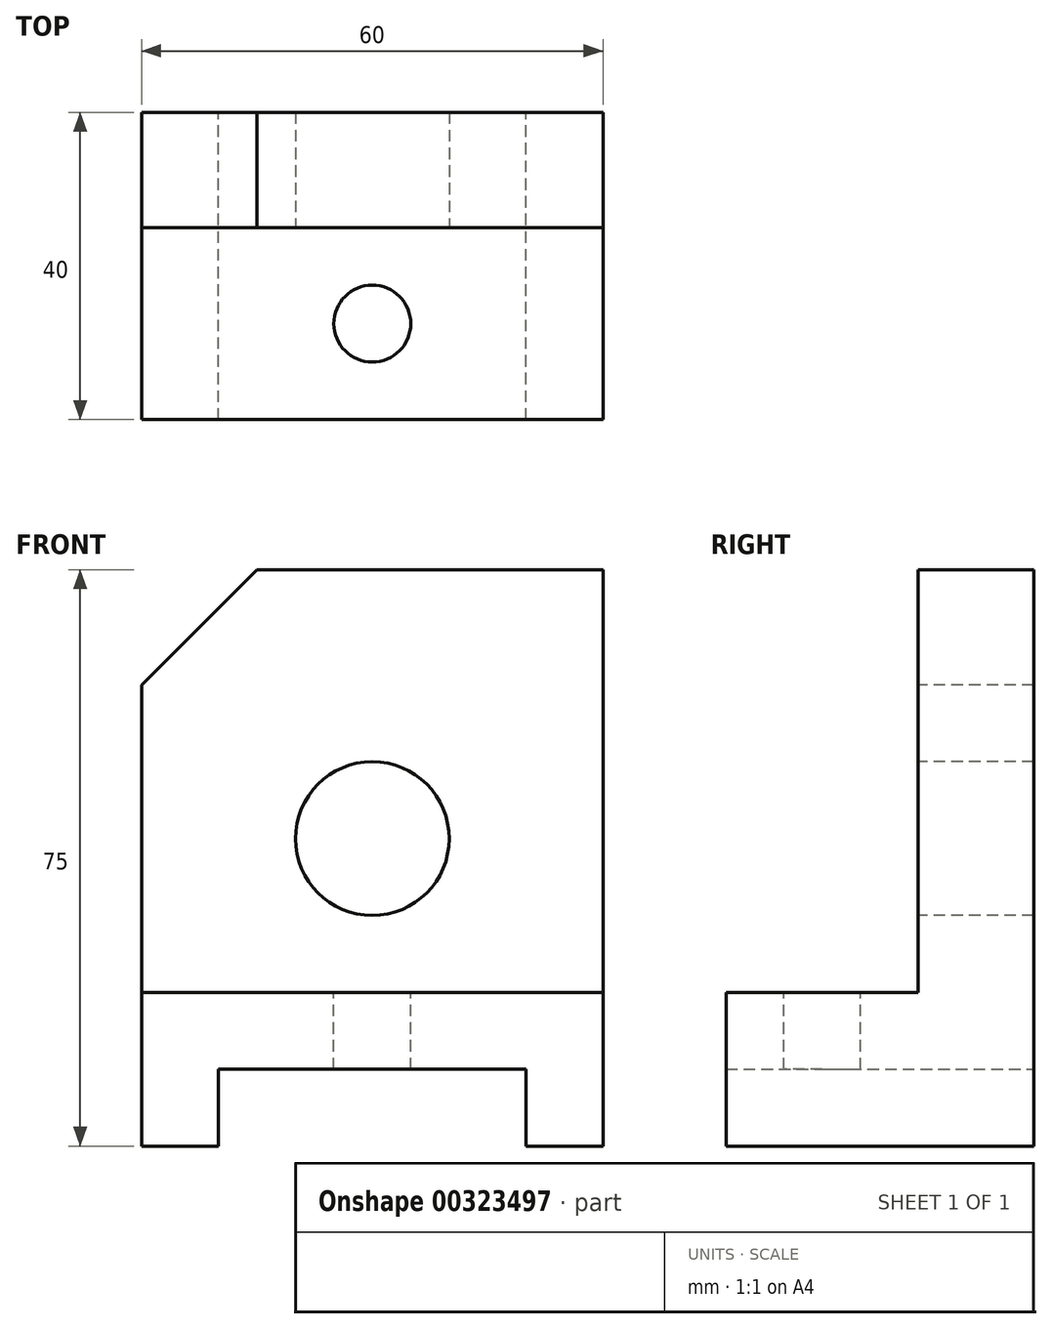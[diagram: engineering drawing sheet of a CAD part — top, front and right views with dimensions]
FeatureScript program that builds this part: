
annotation { "Feature Type Name" : "Feature", "Feature Type Description" : "" }
export const myFeature = defineFeature(function(context is Context, id is Id, definition is map)
    precondition{}
    {
        {
            var Q0;
            Q0=qCreatedBy(makeId("Front.planeOp"),FACE);
            var sketch = newSketch(context, id + "F0", { "sketchPlane" : qUnion([Q0])});
            skLineSegment(sketch, "E0", {"start": v(-30, 0) * mm, "end": v(-30, 20) * mm});
            skLineSegment(sketch, "E1", {"start": v(-30, 20) * mm, "end": v(30, 20) * mm});
            skLineSegment(sketch, "E2", {"start": v(30, 20) * mm, "end": v(30, 0) * mm});
            skLineSegment(sketch, "E3", {"start": v(30, 0) * mm, "end": v(20, 0) * mm});
            skLineSegment(sketch, "E4", {"start": v(20, 0) * mm, "end": v(20, 10) * mm});
            skLineSegment(sketch, "E5", {"start": v(20, 10) * mm, "end": v(-20, 10) * mm});
            skLineSegment(sketch, "E6", {"start": v(-20, 10) * mm, "end": v(-20, 0) * mm});
            skLineSegment(sketch, "E7", {"start": v(-20, 0) * mm, "end": v(-30, 0) * mm});
            skSolve(sketch);
        }
        {
            var Q0;
            Q0=makeQuery(id+"F0.imprint","IMPRINT",FACE,{"disambiguationData":[TD([[makeQuery(id+"F0.imprint","IMPRINT",EDGE,{"derivedFrom":sQuery(id+"F0.wireOp",EDGE,"E0")}),-1.0]])]});
            extrude(context, id + "F1", {"entities" : qUnion([Q0]), "depth" : 40 * mm});
        }
        {
            var Q0;
            Q0=makeQuery(id+"F1.opExtrude","SWEPT_FACE",FACE,{"disambiguationData":[OSD([sQuery(id+"F0.wireOp",EDGE,"E1")])]});
            var sketch = newSketch(context, id + "F2", { "sketchPlane" : qUnion([Q0])});
            skLineSegment(sketch, "E8.bottom", {"start": v(-30, 0) * mm, "end": v(30, 0) * mm});
            skLineSegment(sketch, "E8.top", {"start": v(-30, -15) * mm, "end": v(30, -15) * mm});
            skLineSegment(sketch, "E8.left", {"start": v(-30, 0) * mm, "end": v(-30, -15) * mm});
            skLineSegment(sketch, "E8.right", {"start": v(30, 0) * mm, "end": v(30, -15) * mm});
            skSolve(sketch);
        }
        {
            var Q0;
            Q0 = qSketchRegion(id + "F2", true);
            extrude(context, id + "F3", {"entities" : qUnion([Q0]), "operationType" : NewBodyOperationType.ADD, "depth" : 55 * mm});
        }
        {
            var Q0;
            Q0=makeQuery(id+"F3.opExtrude","SWEPT_FACE",FACE,{"disambiguationData":[OSD([sQuery(id+"F2.wireOp",EDGE,"E8.top")])]});
            var sketch = newSketch(context, id + "F4", { "sketchPlane" : qUnion([Q0])});
            skLineSegment(sketch, "E9", {"start": v(-15, 75) * mm, "end": v(-30, 60) * mm});
            skLineSegment(sketch, "E10", {"start": v(-30, 60) * mm, "end": v(-30, 75) * mm});
            skLineSegment(sketch, "E11", {"start": v(-30, 75) * mm, "end": v(-15, 75) * mm});
            skSolve(sketch);
        }
        {
            var Q0;
            Q0=makeQuery(id+"F4.imprint","IMPRINT",FACE,{"disambiguationData":[TD([[makeQuery(id+"F4.imprint","IMPRINT",EDGE,{"derivedFrom":sQuery(id+"F4.wireOp",EDGE,"E9")}),-1.0]])]});
            extrude(context, id + "F5", {"entities" : qUnion([Q0]), "operationType" : NewBodyOperationType.REMOVE, "oppositeDirection" : true, "depth" : 38.1 * mm});
        }
        {
            var Q0;
            Q0=makeQuery(id+"F3.opExtrude","SWEPT_FACE",FACE,{"disambiguationData":[OSD([sQuery(id+"F2.wireOp",EDGE,"E8.top")])]});
            var sketch = newSketch(context, id + "F6", { "sketchPlane" : qUnion([Q0])});
            skCircle(sketch, "E12", {"center": v(0, 40) * mm, "radius": 10 * mm});
            skSolve(sketch);
        }
        {
            var Q0;
            Q0=makeQuery(id+"F6.imprint","IMPRINT",FACE,{"disambiguationData":[TD([[makeQuery(id+"F6.imprint","IMPRINT",EDGE,{"derivedFrom":sQuery(id+"F6.wireOp",EDGE,"E12")}),1.0]])]});
            extrude(context, id + "F7", {"entities" : qUnion([Q0]), "operationType" : NewBodyOperationType.REMOVE, "oppositeDirection" : true, "depth" : 25.4 * mm});
        }
        {
            var Q0;
            Q0=makeQuery(id+"F1.opExtrude","SWEPT_FACE",FACE,{"disambiguationData":[OSD([sQuery(id+"F0.wireOp",EDGE,"E1")])]});
            var sketch = newSketch(context, id + "F8", { "sketchPlane" : qUnion([Q0])});
            skCircle(sketch, "E13", {"center": v(0, -27.5) * mm, "radius": 5 * mm});
            skSolve(sketch);
        }
        {
            var Q0;
            Q0=makeQuery(id+"F8.imprint","IMPRINT",FACE,{"disambiguationData":[TD([[makeQuery(id+"F8.imprint","IMPRINT",EDGE,{"derivedFrom":sQuery(id+"F8.wireOp",EDGE,"E13")}),1.0]])]});
            extrude(context, id + "F9", {"entities" : qUnion([Q0]), "operationType" : NewBodyOperationType.REMOVE, "oppositeDirection" : true, "depth" : 25.4 * mm});
        }
    });
